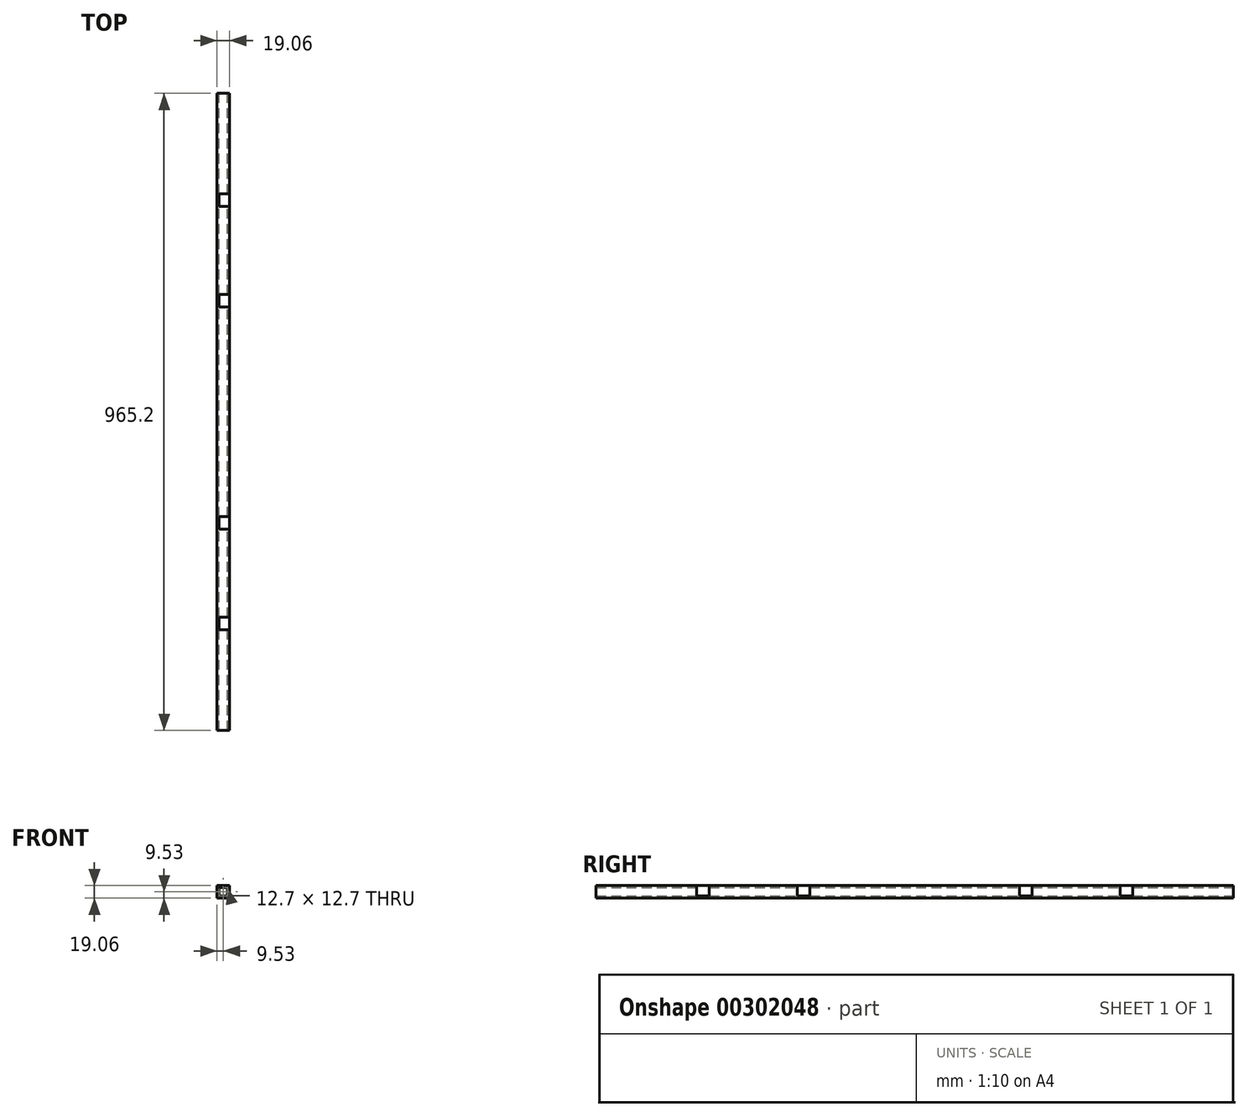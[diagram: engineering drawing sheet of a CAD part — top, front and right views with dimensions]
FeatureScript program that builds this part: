
annotation { "Feature Type Name" : "Feature", "Feature Type Description" : "" }
export const myFeature = defineFeature(function(context is Context, id is Id, definition is map)
    precondition{}
    {
        {
            var Q0;
            Q0=qCreatedBy(makeId("Front.planeOp"),FACE);
            var sketch = newSketch(context, id + "F0", { "sketchPlane" : qUnion([Q0])});
            skLineSegment(sketch, "E0.bottom", {"start": v(9.53, 9.53) * mm, "end": v(-9.53, 9.53) * mm});
            skLineSegment(sketch, "E0.top", {"start": v(9.53, -9.53) * mm, "end": v(-9.53, -9.53) * mm});
            skLineSegment(sketch, "E0.left", {"start": v(9.53, 9.53) * mm, "end": v(9.53, -9.53) * mm});
            skLineSegment(sketch, "E0.right", {"start": v(-9.53, 9.53) * mm, "end": v(-9.53, -9.53) * mm});
            skPoint(sketch, "E0.middle", {"position": v(0, 0) * mm});
            skLineSegment(sketch, "E1.bottom", {"start": v(6.35, 6.35) * mm, "end": v(-6.35, 6.35) * mm});
            skLineSegment(sketch, "E1.top", {"start": v(6.35, -6.35) * mm, "end": v(-6.35, -6.35) * mm});
            skLineSegment(sketch, "E1.left", {"start": v(6.35, 6.35) * mm, "end": v(6.35, -6.35) * mm});
            skLineSegment(sketch, "E1.right", {"start": v(-6.35, 6.35) * mm, "end": v(-6.35, -6.35) * mm});
            skSolve(sketch);
        }
        {
            var Q0;
            Q0 = qSketchRegion(id + "F0", true);
            extrude(context, id + "F1", {"entities" : qUnion([Q0]), "depth" : 965.2 * mm, "offsetDistance" : 25.4 * mm});
        }
        {
            var Q0;
            Q0=makeQuery(id+"F1.opExtrude","SWEPT_FACE",FACE,{"disambiguationData":[OSD([sQuery(id+"F0.wireOp",EDGE,"E0.bottom")])]});
            var sketch = newSketch(context, id + "F2", { "sketchPlane" : qUnion([Q0])});
            skLineSegment(sketch, "E2.bottom", {"start": v(9.52, -152.4) * mm, "end": v(-6.35, -152.4) * mm});
            skLineSegment(sketch, "E2.top", {"start": v(9.52, -171.45) * mm, "end": v(-6.35, -171.45) * mm});
            skLineSegment(sketch, "E2.left", {"start": v(9.52, -152.4) * mm, "end": v(9.52, -171.45) * mm});
            skLineSegment(sketch, "E2.right", {"start": v(-6.35, -152.4) * mm, "end": v(-6.35, -171.45) * mm});
            skLineSegment(sketch, "E3.bottom", {"start": v(9.53, -304.8) * mm, "end": v(-6.35, -304.8) * mm});
            skLineSegment(sketch, "E3.top", {"start": v(9.53, -323.85) * mm, "end": v(-6.35, -323.85) * mm});
            skLineSegment(sketch, "E3.left", {"start": v(9.53, -304.8) * mm, "end": v(9.53, -323.85) * mm});
            skLineSegment(sketch, "E3.right", {"start": v(-6.35, -304.8) * mm, "end": v(-6.35, -323.85) * mm});
            skLineSegment(sketch, "E4.bottom", {"start": v(9.53, -641.35) * mm, "end": v(-6.35, -641.35) * mm});
            skLineSegment(sketch, "E4.top", {"start": v(9.52, -660.4) * mm, "end": v(-6.35, -660.4) * mm});
            skLineSegment(sketch, "E4.left", {"start": v(9.52, -641.35) * mm, "end": v(9.52, -660.4) * mm});
            skLineSegment(sketch, "E4.right", {"start": v(-6.35, -641.35) * mm, "end": v(-6.35, -660.4) * mm});
            skLineSegment(sketch, "E5.bottom", {"start": v(9.53, -812.8) * mm, "end": v(-6.35, -812.8) * mm});
            skLineSegment(sketch, "E5.top", {"start": v(9.52, -793.75) * mm, "end": v(-6.35, -793.75) * mm});
            skLineSegment(sketch, "E5.left", {"start": v(9.52, -812.8) * mm, "end": v(9.52, -793.75) * mm});
            skLineSegment(sketch, "E5.right", {"start": v(-6.35, -812.8) * mm, "end": v(-6.35, -793.75) * mm});
            skSolve(sketch);
        }
        {
            var Q0;
            Q0=makeQuery(id+"F2.imprint","IMPRINT",FACE,{"disambiguationData":[TD([[makeQuery(id+"F2.imprint","IMPRINT",EDGE,{"derivedFrom":sQuery(id+"F2.wireOp",EDGE,"E5.bottom")}),-1.0]])]});
            var Q1;
            Q1=makeQuery(id+"F2.imprint","IMPRINT",FACE,{"disambiguationData":[TD([[makeQuery(id+"F2.imprint","IMPRINT",EDGE,{"derivedFrom":sQuery(id+"F2.wireOp",EDGE,"E4.bottom")}),1.0]])]});
            var Q2;
            Q2=makeQuery(id+"F2.imprint","IMPRINT",FACE,{"disambiguationData":[TD([[makeQuery(id+"F2.imprint","IMPRINT",EDGE,{"derivedFrom":sQuery(id+"F2.wireOp",EDGE,"E3.bottom")}),1.0]])]});
            var Q3;
            Q3=makeQuery(id+"F2.imprint","IMPRINT",FACE,{"disambiguationData":[TD([[makeQuery(id+"F2.imprint","IMPRINT",EDGE,{"derivedFrom":sQuery(id+"F2.wireOp",EDGE,"E2.bottom")}),1.0]])]});
            extrude(context, id + "F3", {"entities" : qUnion([Q0, Q1, Q2, Q3]), "operationType" : NewBodyOperationType.REMOVE, "oppositeDirection" : true, "depth" : 15.88 * mm});
        }
    });
